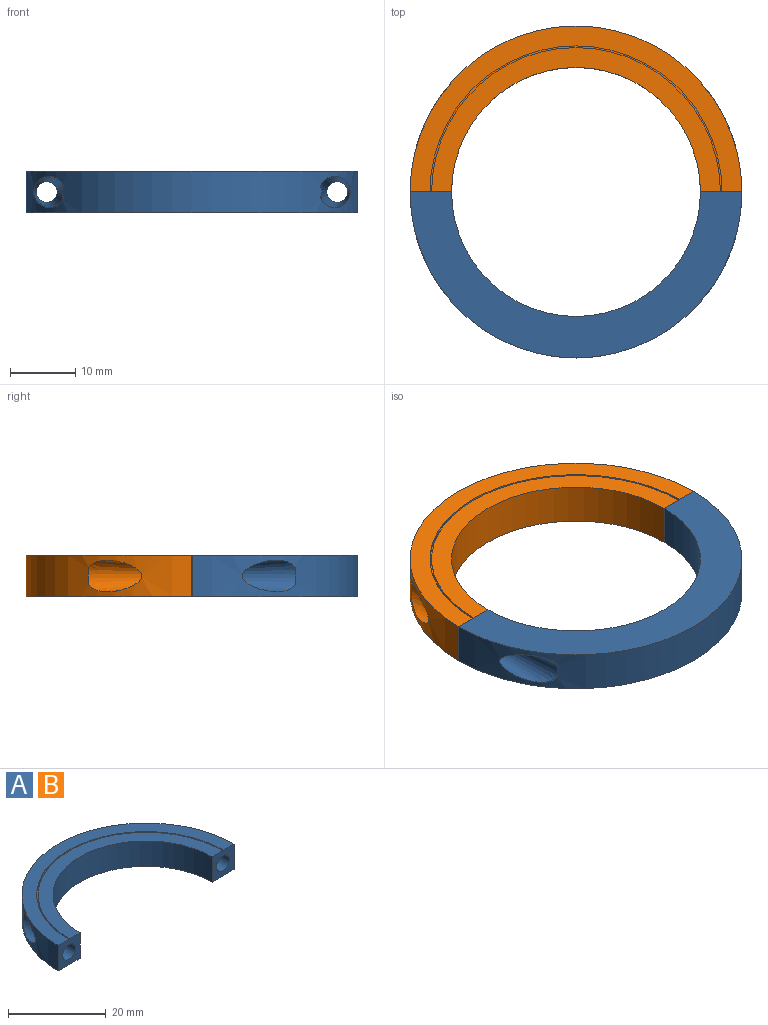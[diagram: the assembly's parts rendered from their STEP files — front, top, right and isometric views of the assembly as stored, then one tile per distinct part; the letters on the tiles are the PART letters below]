
ASSEMBLY  parts=2 mates=1
PART A: 16 faces, bbox 50.8x25.4x6.4 mm
  f0: plane 6.35x6.35mm, normal (0,-1,0), area 29.3mm2, adj f1,f2,f3,f5,f6,f12,f13,f14
  f1: plane 50.8x25.4mm, normal (0,0,1), area 228.6mm2, adj f0,f4,f5,f13
  f2: plane 44.2x22.1mm, normal (0,0,1), area 197mm2, adj f0,f3,f4,f14
  f3: cylinder r=19.05mm len=38.1mm, axis (0,0,-1), area 380mm2, adj f0,f2,f4,f6
  f4: plane 6.35x6.35mm, normal (0,-1,0), area 29.3mm2, adj f1,f2,f3,f5,f6,f7,f13,f14
  f5: cylinder r=25.4mm len=50.8mm, axis (0,0,-1), area 434.8mm2, adj f0,f1,f4,f6,f8,f9,f10,f11
  f6: plane 50.8x25.4mm, normal (0,0,-1), area 443.4mm2, adj f0,f3,f4,f5
  f7: cone r=1.59mm half-angle=5deg, axis (0,-1,0), area 34.6mm2, adj f4,f8
  f8: cone r=1.59mm half-angle=5deg, axis (0,1,0), area 113.8mm2, adj f5,f7,f9
  f9: plane 2.48x0.3mm, normal (0,-1,0), area 0.5mm2, adj f5,f8
  f10: cone r=1.59mm half-angle=5deg, axis (0,1,0), area 113.8mm2, adj f5,f11,f12
  f11: plane 2.48x0.3mm, normal (0,-1,0), area 0.5mm2, adj f5,f10
  f12: cone r=1.59mm half-angle=5deg, axis (0,-1,0), area 34.6mm2, adj f0,f10
  f13: cylinder r=22.35mm len=44.7mm, axis (0,0,1), area 17.8mm2, adj f0,f1,f4,f15
  f14: cylinder r=22.1mm len=44.2mm, axis (0,0,1), area 17.6mm2, adj f0,f2,f4,f15
  f15: plane 44.7x22.35mm, normal (0,0,1), area 17.7mm2, adj f0,f4,f13,f14
PART B: same geometry as A
PLACE A rot(axis=(1,0,0),180deg) t=(-17.95,12.94,2.48)mm
PLACE B t=(-17.95,12.94,-3.87)mm
MATE revolute B.f7 <-> A.f7  axis (0,-1,0) through (4.28,12.94,-0.7)mm
